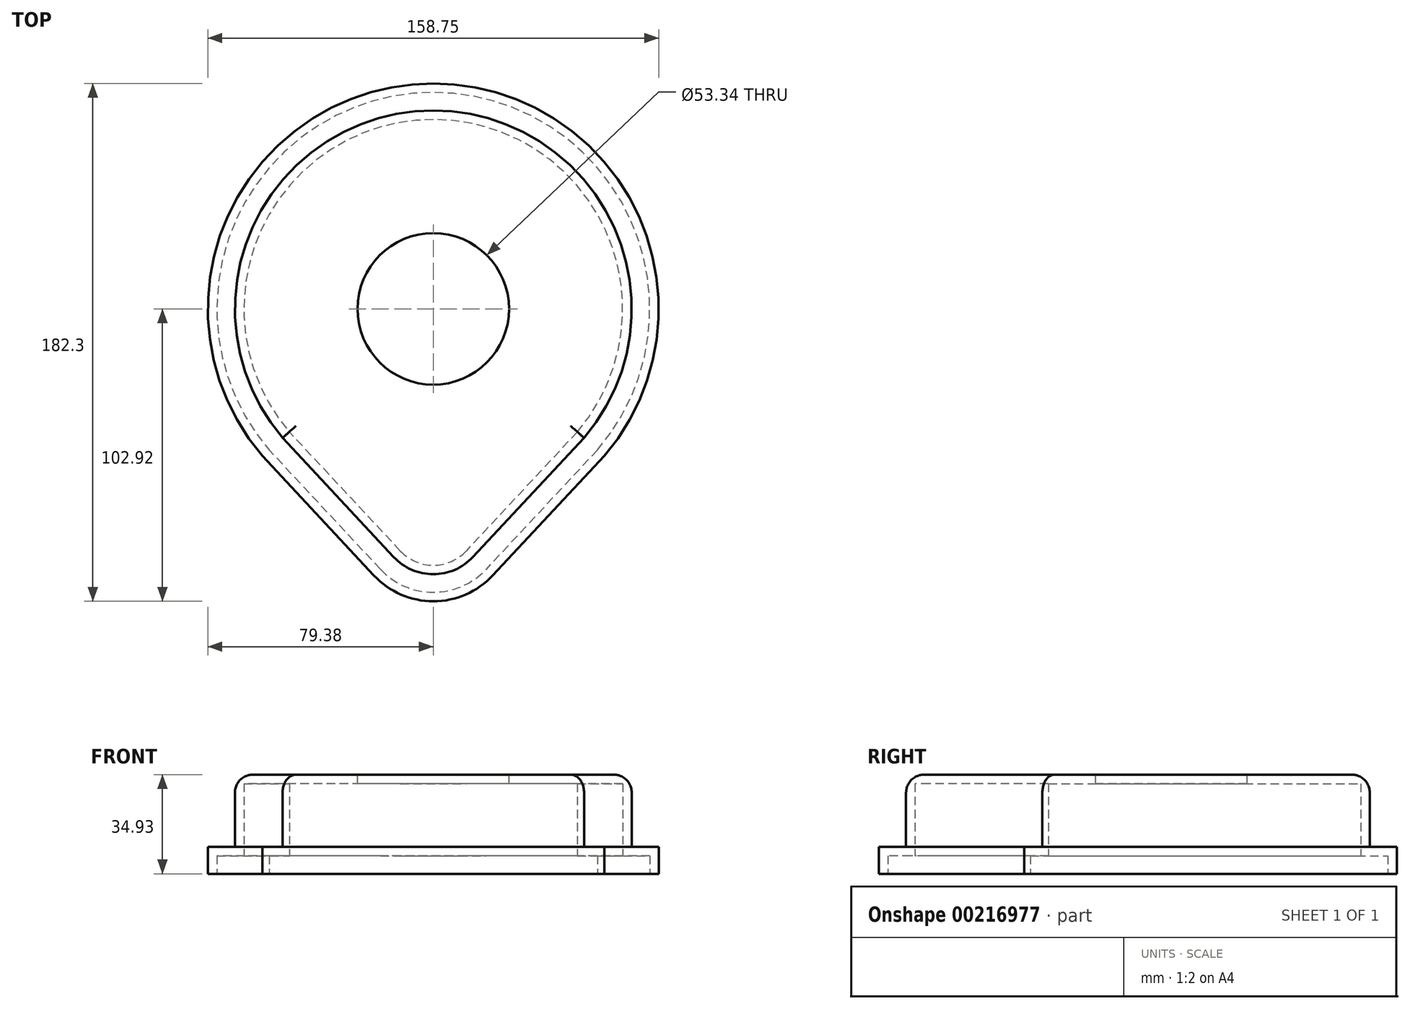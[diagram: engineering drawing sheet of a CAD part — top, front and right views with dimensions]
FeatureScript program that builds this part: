
annotation { "Feature Type Name" : "Feature", "Feature Type Description" : "" }
export const myFeature = defineFeature(function(context is Context, id is Id, definition is map)
    precondition{}
    {
        {
            var Q0;
            Q0=qCreatedBy(makeId("Top.planeOp"),FACE);
            var sketch = newSketch(context, id + "F0", { "sketchPlane" : qUnion([Q0])});
            skArc(sketch, "E0", {"start": v(53.5, -54.27) * mm, "mid": v(0, 76.2) * mm, "end": v(-53.5, -54.27) * mm});
            skLineSegment(sketch, "E1", {"start": v(-18.57, -91.68) * mm, "end": v(-57.81, -49.64) * mm});
            skLineSegment(sketch, "E2", {"start": v(57.81, -49.64) * mm, "end": v(18.57, -91.68) * mm});
            skArc(sketch, "E3.trimOffspring", {"start": v(-18.57, -91.68) * mm, "mid": v(0, -99.75) * mm, "end": v(18.57, -91.68) * mm});
            skArc(sketch, "E4.0", {"start": v(46.8, -47.49) * mm, "mid": v(0, 66.67) * mm, "end": v(-46.8, -47.49) * mm});
            skLineSegment(sketch, "E5.0", {"start": v(-11.6, -85.18) * mm, "end": v(-50.85, -43.14) * mm});
            skArc(sketch, "E5.1", {"start": v(-11.6, -85.18) * mm, "mid": v(0, -90.22) * mm, "end": v(11.6, -85.18) * mm});
            skLineSegment(sketch, "E5.2", {"start": v(50.85, -43.14) * mm, "end": v(11.6, -85.18) * mm});
            skSolve(sketch);
        }
        {
            var Q0;
            {var subQ5=sQuery(id+"F0.wireOp",EDGE,"E5.1");Q0=makeQuery(id+"F0.imprint","IMPRINT",FACE,{"disambiguationData":[TD([[makeQuery(id+"F0.imprint","IMPRINT",EDGE,{"derivedFrom":subQ5}),1.0]])]});}
            extrude(context, id + "F1", {"entities" : qUnion([Q0]), "depth" : 31.75 * mm});
        }
        {
            var Q0;
            {var subQ7=sQuery(id+"F0.wireOp",EDGE,"E3.trimOffspring");Q0=makeQuery(id+"F0.imprint","IMPRINT",FACE,{"disambiguationData":[TD([[makeQuery(id+"F0.imprint","IMPRINT",EDGE,{"derivedFrom":subQ7}),1.0]])]});}
            extrude(context, id + "F2", {"entities" : qUnion([Q0]), "operationType" : NewBodyOperationType.ADD, "depth" : 6.35 * mm});
        }
        {
            var Q0;
            {var subQ0=sQuery(id+"F0.wireOp",EDGE,"E5.2");var subQ1=sQuery(id+"F0.wireOp",EDGE,"E5.1");var subQ2=sQuery(id+"F0.wireOp",EDGE,"E5.0");var subQ3=sQuery(id+"F0.wireOp",EDGE,"E4.0");Q0=makeQuery(id+"F2.boolean.opBoolean","MERGE",FACE,{"derivedFrom":[makeQuery(id+"F1.opExtrude","CAP_FACE",FACE,{"disambiguationData":[OSD([subQ3,subQ2,subQ1,subQ0])],"isStart":true}),makeQuery(id+"F2.opExtrude","CAP_FACE",FACE,{"disambiguationData":[OSD([sQuery(id+"F0.wireOp",EDGE,"E0"),sQuery(id+"F0.wireOp",EDGE,"E1"),sQuery(id+"F0.wireOp",EDGE,"E2"),sQuery(id+"F0.wireOp",EDGE,"E3.trimOffspring"),subQ3,subQ2,subQ1,subQ0])],"isStart":true})]});}
            shell(context, id + "F3", {"entities" : qUnion([Q0]), "thickness" : 3.17 * mm, "oppositeDirection" : true});
        }
        {
            var Q0;
            Q0=makeQuery(id+"F1.opExtrude","CAP_FACE",FACE,{"disambiguationData":[OSD([sQuery(id+"F0.wireOp",EDGE,"E4.0"),sQuery(id+"F0.wireOp",EDGE,"E5.0"),sQuery(id+"F0.wireOp",EDGE,"E5.1"),sQuery(id+"F0.wireOp",EDGE,"E5.2")])],"isStart":false});
            fillet(context, id + "F4", {"entities" : qUnion([Q0]), "radius" : 6.35 * mm, "tangentPropagation" : true, "allowEdgeOverflow" : false});
        }
        {
            var Q0;
            Q0=makeQuery(id+"F1.opExtrude","CAP_FACE",FACE,{"disambiguationData":[OSD([sQuery(id+"F0.wireOp",EDGE,"E4.0"),sQuery(id+"F0.wireOp",EDGE,"E5.0"),sQuery(id+"F0.wireOp",EDGE,"E5.1"),sQuery(id+"F0.wireOp",EDGE,"E5.2")])],"isStart":false});
            var sketch = newSketch(context, id + "F5", { "sketchPlane" : qUnion([Q0])});
            skCircle(sketch, "E6", {"center": v(0, 0) * mm, "radius": 26.67 * mm});
            skSolve(sketch);
        }
        {
            var Q0;
            Q0=makeQuery(id+"F5.imprint","IMPRINT",FACE,{"disambiguationData":[TD([[makeQuery(id+"F5.imprint","IMPRINT",EDGE,{"derivedFrom":sQuery(id+"F5.wireOp",EDGE,"E6")}),1.0]])]});
            extrude(context, id + "F6", {"entities" : qUnion([Q0]), "operationType" : NewBodyOperationType.REMOVE, "oppositeDirection" : true, "depth" : 25.4 * mm});
        }
    });
